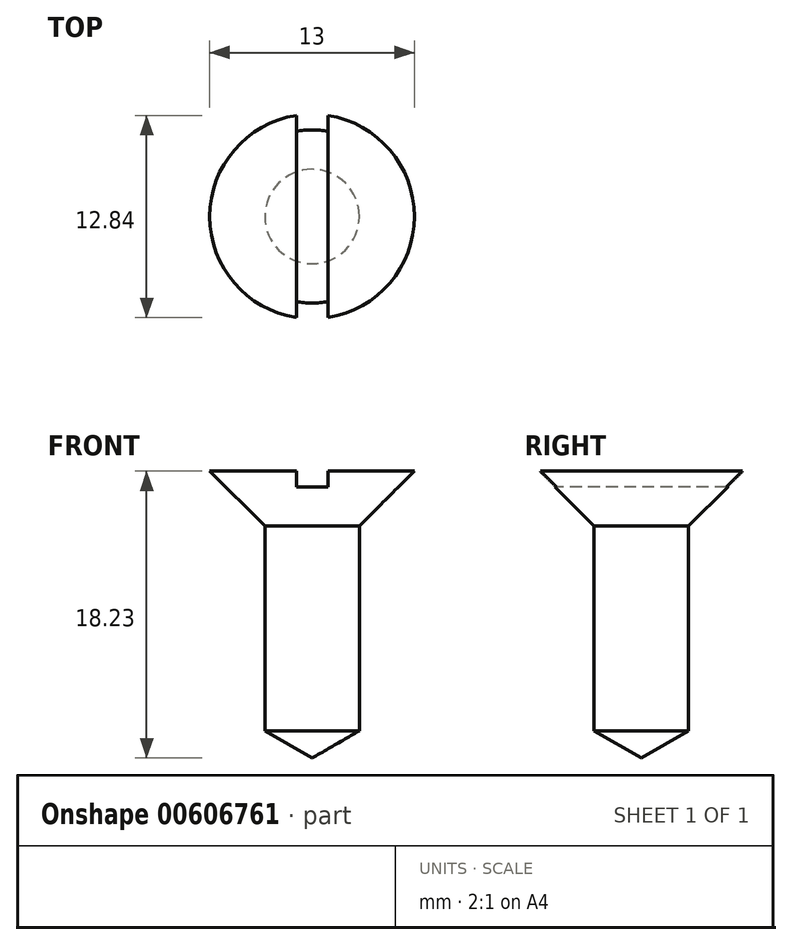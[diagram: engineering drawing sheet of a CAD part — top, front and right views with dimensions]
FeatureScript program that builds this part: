
annotation { "Feature Type Name" : "Feature", "Feature Type Description" : "" }
export const myFeature = defineFeature(function(context is Context, id is Id, definition is map)
    precondition{}
    {
        {
            var Q0;
            Q0=qCreatedBy(makeId("Front.planeOp"),FACE);
            var sketch = newSketch(context, id + "F0", { "sketchPlane" : qUnion([Q0])});
            skLineSegment(sketch, "E0", {"start": v(0, 0) * mm, "end": v(3, 1.73) * mm});
            skLineSegment(sketch, "E1", {"start": v(3, 1.73) * mm, "end": v(3, 14.73) * mm});
            skLineSegment(sketch, "E2", {"start": v(3, 14.73) * mm, "end": v(6.5, 18.23) * mm});
            skLineSegment(sketch, "E3", {"start": v(6.5, 18.23) * mm, "end": v(0, 18.23) * mm});
            skLineSegment(sketch, "E4", {"start": v(0, 18.23) * mm, "end": v(0, 0) * mm});
            skSolve(sketch);
        }
        {
            var Q0;
            Q0=makeQuery(id+"F0.imprint","IMPRINT",FACE,{"disambiguationData":[TD([[makeQuery(id+"F0.imprint","IMPRINT",EDGE,{"derivedFrom":sQuery(id+"F0.wireOp",EDGE,"E0")}),1.0]])]});
            var Q1;
            Q1=sQuery(id+"F0.wireOp",EDGE,"E4");
            revolve(context, id + "F1", {"entities" : qUnion([Q0]), "axis" : qUnion([Q1]), "revolveType" : RevolveType.FULL});
        }
        {
            var Q0;
            Q0=qCreatedBy(makeId("Front.planeOp"),FACE);
            var sketch = newSketch(context, id + "F2", { "sketchPlane" : qUnion([Q0])});
            skLineSegment(sketch, "E5.bottom", {"start": v(1, 22.14) * mm, "end": v(-1, 22.14) * mm});
            skLineSegment(sketch, "E5.top", {"start": v(1, 17.23) * mm, "end": v(-1, 17.23) * mm});
            skLineSegment(sketch, "E5.left", {"start": v(1, 22.14) * mm, "end": v(1, 17.23) * mm});
            skLineSegment(sketch, "E5.right", {"start": v(-1, 22.14) * mm, "end": v(-1, 17.23) * mm});
            skPoint(sketch, "E5.middle", {"position": v(0, 19.68) * mm});
            skSolve(sketch);
        }
        {
            var Q0;
            Q0=makeQuery(id+"F2.imprint","IMPRINT",FACE,{"disambiguationData":[TD([[makeQuery(id+"F2.imprint","IMPRINT",EDGE,{"derivedFrom":sQuery(id+"F2.wireOp",EDGE,"E5.bottom")}),1.0]])]});
            extrude(context, id + "F3", {"entities" : qUnion([Q0]), "operationType" : NewBodyOperationType.REMOVE, "endBound" : BoundingType.THROUGH_ALL, "oppositeDirection" : true, "depth" : 25 * mm, "offsetDistance" : 25 * mm, "hasSecondDirection" : true, "secondDirectionBound" : SecondDirectionBoundingType.THROUGH_ALL, "secondDirectionOppositeDirection" : false, "secondDirectionDepth" : 25 * mm});
        }
    });
